# Revit family: Franke_Kartenleser-A200
name_source: partatom
category: Sonderausstattung
revit_build: Autodesk Revit 2015 (Build: 20140606_1530(x64)
units: mm (PartAtom-declared; Revit-internal decimal feet)

## types (2) — shared parameters
Anzahl der Nullleiter = 1
Anzahl der Schutzleiter = 1
Anzahl von Polen = 1
Aufstellgewicht = 18 kg
Bauelement = Beistellgehäuse für Wert- und Geldkartensyteme
Baugruppenkennzeichen = Beistellgehäuse für Wert- und Geldkartensyteme
Beschreibung = Beistellgehäuse ist für die Integration eines bauseitig vorhandenen Wert- oder Geldkartenleser vorbereitet
Breite = 200 mm  [stored 0.656168 ft]
Energieverlust nach DIN18873 = k.A.
Hersteller = Franke
Höhe = 544 mm
Leistung = Leistung systemabhängig
Modell = 410905 - Kartenleser-A200
Netzfrequenz = 50 Hz
Netzfrequenz alternativ = 60 Hz
Spannung max. = 264 V
Spannung min. = 85 V
Tiefe = 452 mm  [stored 1.48294 ft]
URL = http://www.franke.com
zero-valued in all types: Kosten

## per-type parameters (varying)
| type | Abdeckung |
| Kartenleser-A200(85-264V/black line/EU) | Franke Black |
| Kartenleser-A200(85-264V/anthrazit/EU) | Franke Anthrazit |

note: [stored X ft] marks values corroborated as IEEE doubles in the binary element streams (Revit-internal decimal feet)
